# Revit family: Grohe_PlumbingFixtures_Eurosmart_SingleLeverShowerMixer_19451003xxx
name_source: partatom
category: Plumbing Fixtures
revit_build: Autodesk Revit 2018 (Build: 20190510_1515(x64)
units: mm (PartAtom-declared; Revit-internal decimal feet)

## family parameters
Cut with Voids When Loaded = No
Host = Face
OmniClass Number = 23.65.00.00
OmniClass Title = Supply and Distribution of Liquids and Gases
Part Type = Normal
Room Calculation Point = No
Round Connector Dimension = Use Diameter
Shared = No

## types (1)
- 19451003
    Assembly Code = D2010
    AssetType = Fixed
    BIMObjectName = Grohe_PlumbingFixtures_Eurosmart_SingleLeverShowerMixer_19451003
    CO2NeutralProduction = GROHE is one of the first leading manufacturer within the sanitary industry having a CO2-neutral production.
    CW Connection = Yes
    CWFU = 0
    ClassificationName = Uniclass 2015
    ClassificationValue = Pr_40_20_87_55
    Color = Chrome
    Default Elevation = 0 mm  [stored 0 ft]
    Description = Eurosmart single lever shower mixer
    DocumentationCertificates = https://www.bimstore.co
    DocumentationInstallationGuide = https://www.bimstore.co
    DocumentationLiterature = https://www.bimstore.co
    DocumentationMaintenance = https://www.bimstore.co
    DocumentationTechnical = https://www.bimstore.co
    DurationUnit = Year
    EF000010 = Finishing section
    EF002149 = 0
    EF002286 = 0
    EF002671 = Chrome
    EF005464 = 0
    EF014591 = 0
    EF020105 = No
    EF020774 = 0
    EF020775 = 0
    EF020776 = 0
    EF020777 = 0
    EF020778 = 0
    EF020779 = 0
    EF020780 = Single-grip
    EF020781 = Cartouche, ceramic
    EF020782 = Brass
    EF020783 = Chromium-plated
    EF020784 = Polished
    EF020785 = 0
    EF020786 = 1
    EF020788 = 0
    EF020789 = 102 mm
    EF020790 = 0
    EF020963 = 0
    EF021855 = 0
    EF023686 = 0
    EF023687 = 0
    EF023957 = 0
    EFDE0022 = Group I, <=20 dB(A)
    EFSE0002 = 0
    Ecojoy = No
    ExpectedLife = 0
    Features = Final installation for; 33 964 000; without concealed body; GROHE StarLight chrome finish; GROHE FastFixation escutcheon with covered fixation; escutcheon- and shaft-sealing; metal wall escutcheon.
    FullRecyclabilityOfPlastic = All plastic components are fully recyclable
    GROHESocialCommittment = green.grohe.com/social_engagement
    GROHESustainability = green.grohe.com
    HW Connection = Yes
    HWFU = 0
    IfcExportAs = IfcPipeFitting
    IfcExportType = IfcPipeFittingType
    Keynote = N13
    Manufacturer = Grohe
    ManufacturerName = Grohe
    Model = 19451003
    ModelNumber = 19451003
    ModelReference = Single-Lever Shower Mixer
    NBSDescription = Mixer taps
    NBSObjectName = Grohe - Mixer taps
    NBSReference = 45-35-70/345
    NominalDepth = 0 mm  [stored 0 ft]
    NominalHeight = 0 mm  [stored 0 ft]
    NominalLength = 0 mm  [stored 0 ft]
    PrimaryMaterial = Steel, Chrome Plated
    ProductionYear = 2021
    SustainabilityAward = green.grohe.com/awards
    SustainabilityReport = green.grohe.com/reporting
    Type Comments = Single-Lever Shower Mixer
    TypeName = Single-Lever Shower Mixer
    URL = https://www.grohe.co.uk
    Vent Connection = No
    WFU = 0
    WarrantyDurationLabor = 0
    WarrantyDurationParts = 0
    WarrantyDurationUnit = Year
    Waste Connection = No
    _BSBibleVersion = 16
    _BimSpecGuid = 0
    _CurrentRevision = 1
    _DistributedBy = www.bimstore.co
    _ObjectUserGuide = https://www.bimstore.co

note: [stored X ft] marks values corroborated as IEEE doubles in the binary element streams (Revit-internal decimal feet)

## geometry (parser evidence)
native form markers: Sweep x2
no freeform markers — native parametric forms only
